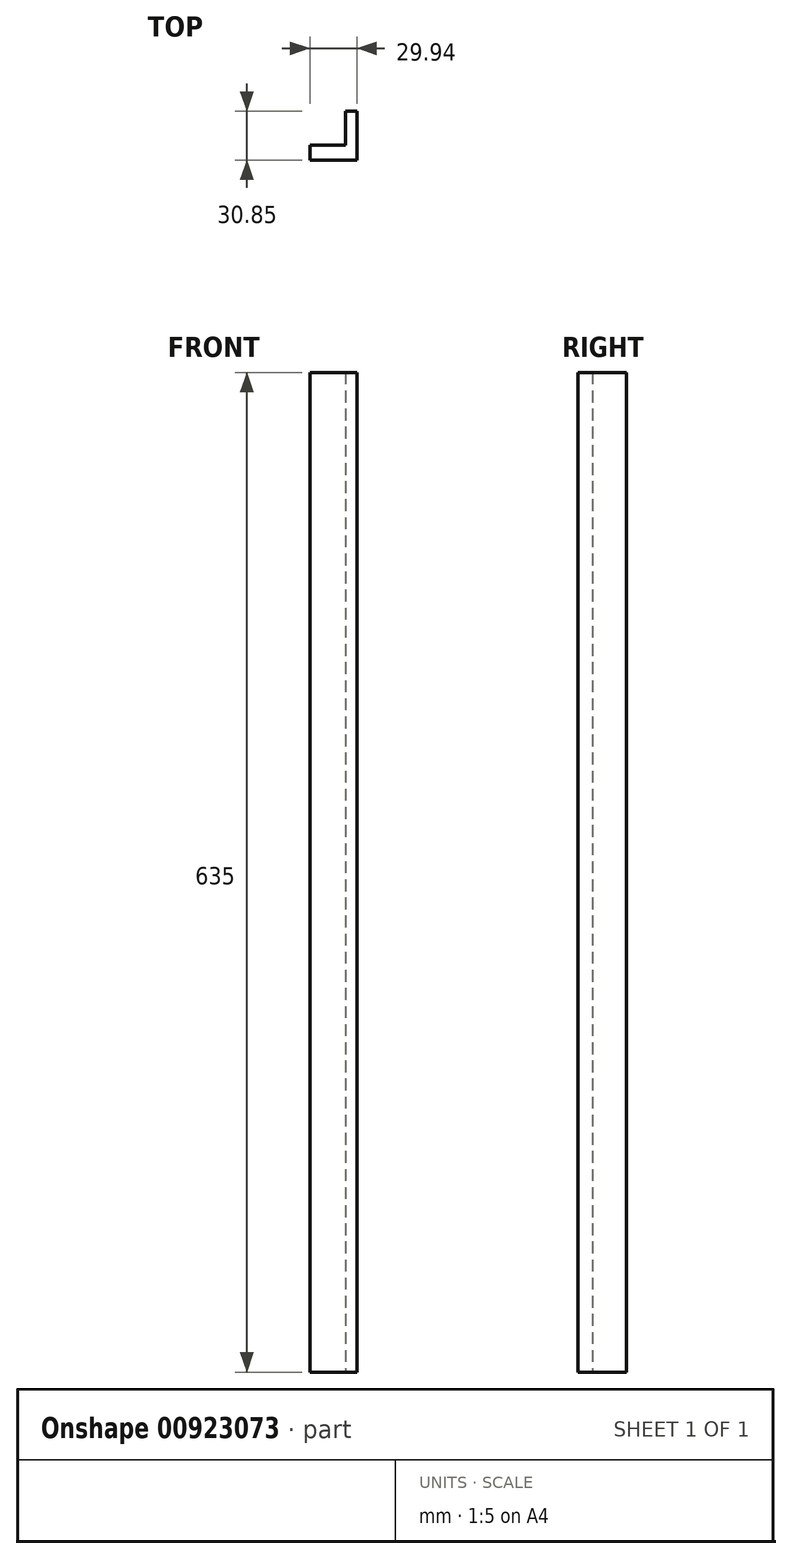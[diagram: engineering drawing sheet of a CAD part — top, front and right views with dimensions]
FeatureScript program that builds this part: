
annotation { "Feature Type Name" : "Feature", "Feature Type Description" : "" }
export const myFeature = defineFeature(function(context is Context, id is Id, definition is map)
    precondition{}
    {
        {
            var Q0;
            Q0=qCreatedBy(makeId("Top.planeOp"),FACE);
            var sketch = newSketch(context, id + "F0", { "sketchPlane" : qUnion([Q0])});
            skLineSegment(sketch, "E0", {"start": v(0, 0) * mm, "end": v(22.75, 0) * mm});
            skLineSegment(sketch, "E1", {"start": v(22.75, 0) * mm, "end": v(22.75, 21.45) * mm});
            skLineSegment(sketch, "E2", {"start": v(22.75, 21.45) * mm, "end": v(29.94, 21.45) * mm});
            skLineSegment(sketch, "E3", {"start": v(29.94, 21.45) * mm, "end": v(29.94, 0) * mm});
            skLineSegment(sketch, "E4", {"start": v(0, 0) * mm, "end": v(0, -9.4) * mm});
            skLineSegment(sketch, "E5", {"start": v(0, -9.4) * mm, "end": v(22.75, -9.4) * mm});
            skLineSegment(sketch, "E6", {"start": v(22.75, -9.4) * mm, "end": v(29.94, -9.4) * mm});
            skLineSegment(sketch, "E7", {"start": v(29.94, -9.4) * mm, "end": v(29.94, 0) * mm});
            skSolve(sketch);
        }
        {
            var Q0;
            Q0 = qSketchRegion(id + "F0", true);
            extrude(context, id + "F1", {"entities" : qUnion([Q0]), "depth" : 25.4 * mm, "offsetDistance" : 25.4 * mm});
        }
        {
            var Q0;
            Q0=makeQuery(id+"F1.opExtrude","CAP_FACE",FACE,{"disambiguationData":[OSD([sQuery(id+"F0.wireOp",EDGE,"E0"),sQuery(id+"F0.wireOp",EDGE,"E1"),sQuery(id+"F0.wireOp",EDGE,"E2"),sQuery(id+"F0.wireOp",EDGE,"E3"),sQuery(id+"F0.wireOp",EDGE,"E4"),sQuery(id+"F0.wireOp",EDGE,"E5"),sQuery(id+"F0.wireOp",EDGE,"E6"),sQuery(id+"F0.wireOp",EDGE,"E7")])],"isStart":false});
            extrude(context, id + "F2", {"entities" : qUnion([Q0]), "operationType" : NewBodyOperationType.ADD, "depth" : 609.6 * mm, "offsetDistance" : 25.4 * mm});
        }
    });
